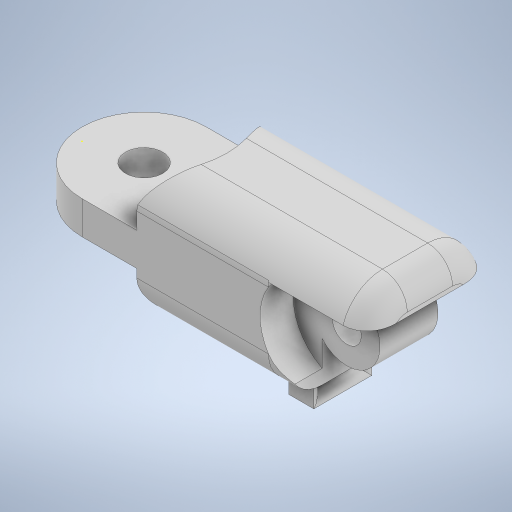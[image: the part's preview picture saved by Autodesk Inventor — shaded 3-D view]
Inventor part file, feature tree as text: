
AUTODESK INVENTOR PART (.ipt)
format: ipt  version: 2024 (Build 280153000, 153)  size: 456,704 bytes
history: native  units: mm
features: sketch x18, extrude x17, fillet x4, other x1
ambient origin geometry x8: Origin, YZ Plane, XZ Plane, XY Plane, X Axis, Y Axis, Z Axis, Center Point
bodies: Body1 (feature_tree)
feature tree (40):
  other  "Твердое тело1"
  extrude  "Выдавливание1"  Depth=15.0mm
  extrude  "Выдавливание2"  Depth=25.0mm
  extrude  "Выдавливание3"  Depth=15.0mm TaperAngle=0.0deg
  extrude  "Выдавливание4"  Depth=5.0mm TaperAngle=0.0deg
  extrude  "Выдавливание5"  Depth=5.0mm TaperAngle=0.0deg
  extrude  "Выдавливание6"  Depth=4.5mm
  extrude  "Выдавливание7"  Depth=5.0mm TaperAngle=0.0deg
  sketch  "Эскиз9"
  extrude  "Выдавливание8"  Depth=8.0mm
  extrude  "Выдавливание9"  Depth=3.0mm
  extrude  "Выдавливание10"  Depth=3.5mm
  extrude  "Выдавливание11"  TaperAngle=0.0deg  [1 undecoded]
  fillet  "Сопряжение6"  Radius=20.0mm
  extrude  "Выдавливание12"  Depth=5.0mm TaperAngle=0.0deg
  extrude  "Выдавливание13"  Depth=20.0mm
  fillet  "Сопряжение7"  Radius=5.0mm
  extrude  "Выдавливание14"  Depth=4.0mm
  extrude  "Выдавливание15"  Depth=0.0mm
  fillet  "Сопряжение8"  [1 undecoded]
  fillet  "Сопряжение9"  Radius=10.0mm
  extrude  "Выдавливание16"  Depth=13.0mm
  extrude  "Выдавливание17"  Depth=13.0mm
  sketch  "Эскиз1"
  sketch  "Эскиз2"
  sketch  "Эскиз3"
  sketch  "Эскиз4"
  sketch  "Эскиз6"
  sketch  "Эскиз7"
  sketch  "Эскиз8"
  sketch  "Эскиз10"
  sketch  "Эскиз12"
  sketch  "Эскиз13"
  sketch  "Эскиз14"
  sketch  "Эскиз15"
  sketch  "Эскиз16"
  sketch  "Эскиз17"
  sketch  "Эскиз18"
  sketch  "Эскиз19"
  sketch  "Эскиз20"
note: 2 required parameter values undecoded (feature->parameter linkage not recoverable at this tier; creation-order binding heuristic only, values carry confidence <= 0.55)
